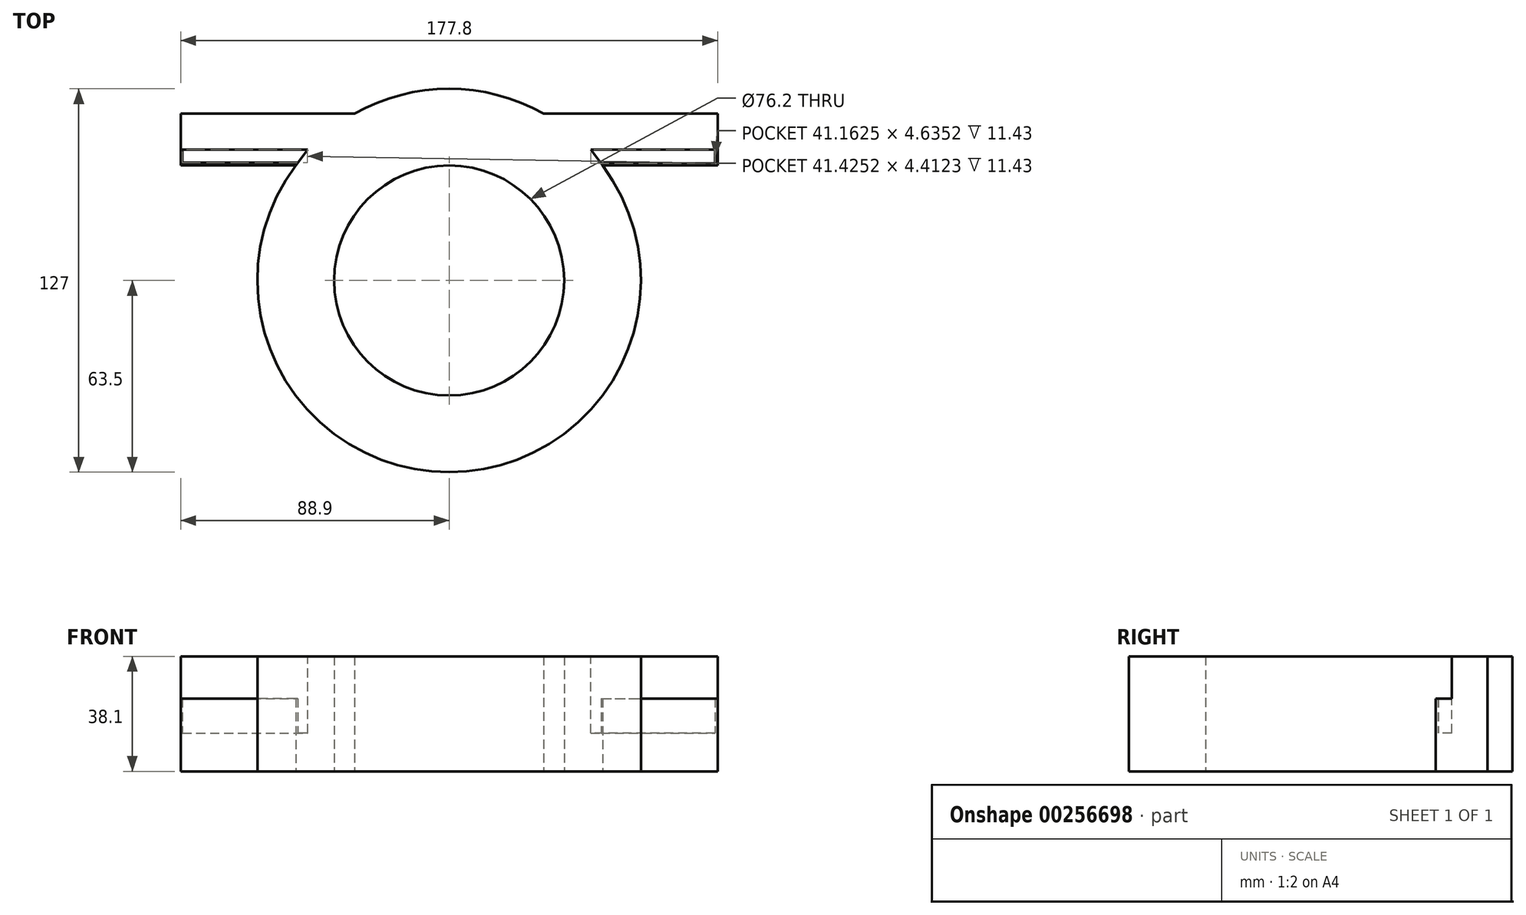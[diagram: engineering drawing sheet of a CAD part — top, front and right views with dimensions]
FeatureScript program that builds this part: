
annotation { "Feature Type Name" : "Feature", "Feature Type Description" : "" }
export const myFeature = defineFeature(function(context is Context, id is Id, definition is map)
    precondition{}
    {
        {
            var Q0;
            Q0=qCreatedBy(makeId("Top.planeOp"),FACE);
            var sketch = newSketch(context, id + "F0", { "sketchPlane" : qUnion([Q0])});
            skCircle(sketch, "E0", {"center": v(0, 0) * mm, "radius": 63.5 * mm});
            skCircle(sketch, "E1", {"center": v(0, 0) * mm, "radius": 38.1 * mm});
            skLineSegment(sketch, "E2.bottom", {"start": v(0, 38.1) * mm, "end": v(88.9, 38.1) * mm});
            skLineSegment(sketch, "E2.top", {"start": v(0, 55.26) * mm, "end": v(88.9, 55.26) * mm});
            skLineSegment(sketch, "E2.left", {"start": v(0, 38.1) * mm, "end": v(0, 55.26) * mm});
            skLineSegment(sketch, "E2.right", {"start": v(88.9, 38.1) * mm, "end": v(88.9, 55.26) * mm});
            skLineSegment(sketch, "E3.bottom", {"start": v(0, 38.1) * mm, "end": v(-88.9, 38.1) * mm});
            skLineSegment(sketch, "E3.top", {"start": v(0, 55.26) * mm, "end": v(-88.9, 55.26) * mm});
            skLineSegment(sketch, "E3.right", {"start": v(-88.9, 38.1) * mm, "end": v(-88.9, 55.26) * mm});
            skSolve(sketch);
        }
        {
            var Q0;
            Q0 = qSketchRegion(id + "F0", true);
            extrude(context, id + "F1", {"entities" : qUnion([Q0]), "depth" : 38.1 * mm});
        }
        {
            var Q0;
            Q0=makeQuery(id+"F1.opExtrude","CAP_FACE",FACE,{"disambiguationData":[OSD([sQuery(id+"F0.wireOp",EDGE,"E0"),sQuery(id+"F0.wireOp",EDGE,"E1"),sQuery(id+"F0.wireOp",EDGE,"E2.bottom"),sQuery(id+"F0.wireOp",EDGE,"E2.top"),sQuery(id+"F0.wireOp",EDGE,"E2.right"),sQuery(id+"F0.wireOp",EDGE,"E3.bottom"),sQuery(id+"F0.wireOp",EDGE,"E3.top"),sQuery(id+"F0.wireOp",EDGE,"E3.right")])],"isStart":false});
            var sketch = newSketch(context, id + "F2", { "sketchPlane" : qUnion([Q0])});
            skLineSegment(sketch, "E4", {"start": v(-88.9, 43.4) * mm, "end": v(-46.87, 43.4) * mm});
            skLineSegment(sketch, "E5", {"start": v(-46.87, 43.4) * mm, "end": v(-50.8, 38.1) * mm});
            skLineSegment(sketch, "E6", {"start": v(-50.8, 38.1) * mm, "end": v(-88.9, 38.1) * mm});
            skLineSegment(sketch, "E7", {"start": v(-88.9, 38.1) * mm, "end": v(-88.9, 43.4) * mm});
            skLineSegment(sketch, "E8", {"start": v(88.9, 43.4) * mm, "end": v(46.86, 43.4) * mm});
            skLineSegment(sketch, "E9", {"start": v(46.86, 43.4) * mm, "end": v(50.8, 38.1) * mm});
            skLineSegment(sketch, "E10", {"start": v(50.8, 38.1) * mm, "end": v(88.9, 38.1) * mm});
            skLineSegment(sketch, "E11", {"start": v(88.9, 38.1) * mm, "end": v(88.9, 43.4) * mm});
            skSolve(sketch);
        }
        {
            var Q0;
            Q0 = qSketchRegion(id + "F2", true);
            extrude(context, id + "F3", {"entities" : qUnion([Q0]), "operationType" : NewBodyOperationType.REMOVE, "oppositeDirection" : true, "depth" : 25.4 * mm});
        }
        {
            var Q0;
            Q0=makeQuery(id+"F3.boolean.opBoolean","COPY",FACE,{"derivedFrom":makeQuery(id+"F3.opExtrude","CAP_FACE",FACE,{"disambiguationData":[OSD([sQuery(id+"F2.wireOp",EDGE,"E8"),sQuery(id+"F2.wireOp",EDGE,"E9"),sQuery(id+"F2.wireOp",EDGE,"E10"),sQuery(id+"F2.wireOp",EDGE,"E11")])],"isStart":false})});
            var sketch = newSketch(context, id + "F4", { "sketchPlane" : qUnion([Q0])});
            skLineSegment(sketch, "E12", {"start": v(-88.3, 38.99) * mm, "end": v(-50.14, 38.99) * mm});
            skLineSegment(sketch, "E13", {"start": v(-50.14, 38.99) * mm, "end": v(-50.8, 38.1) * mm});
            skLineSegment(sketch, "E14", {"start": v(-50.8, 38.1) * mm, "end": v(-88.9, 38.1) * mm});
            skLineSegment(sketch, "E15", {"start": v(-88.9, 38.1) * mm, "end": v(-88.9, 38.99) * mm});
            skLineSegment(sketch, "E16", {"start": v(-88.9, 38.99) * mm, "end": v(-88.9, 43.4) * mm});
            skLineSegment(sketch, "E17", {"start": v(-88.9, 43.4) * mm, "end": v(-88.3, 43.4) * mm});
            skLineSegment(sketch, "E18", {"start": v(-88.3, 43.4) * mm, "end": v(-88.3, 38.99) * mm});
            skLineSegment(sketch, "E19", {"start": v(88.9, 43.4) * mm, "end": v(88.9, 38.1) * mm});
            skLineSegment(sketch, "E20", {"start": v(88.9, 38.1) * mm, "end": v(50.8, 38.1) * mm});
            skLineSegment(sketch, "E21", {"start": v(50.8, 38.1) * mm, "end": v(50.3, 38.77) * mm});
            skLineSegment(sketch, "E22", {"start": v(50.3, 38.77) * mm, "end": v(88.03, 38.77) * mm});
            skLineSegment(sketch, "E23", {"start": v(88.03, 38.77) * mm, "end": v(88.03, 43.4) * mm});
            skLineSegment(sketch, "E24", {"start": v(88.03, 43.4) * mm, "end": v(88.9, 43.4) * mm});
            skSolve(sketch);
        }
        {
            var Q0;
            Q0 = qSketchRegion(id + "F4", true);
            extrude(context, id + "F5", {"entities" : qUnion([Q0]), "operationType" : NewBodyOperationType.ADD, "depth" : 11.43 * mm});
        }
    });
